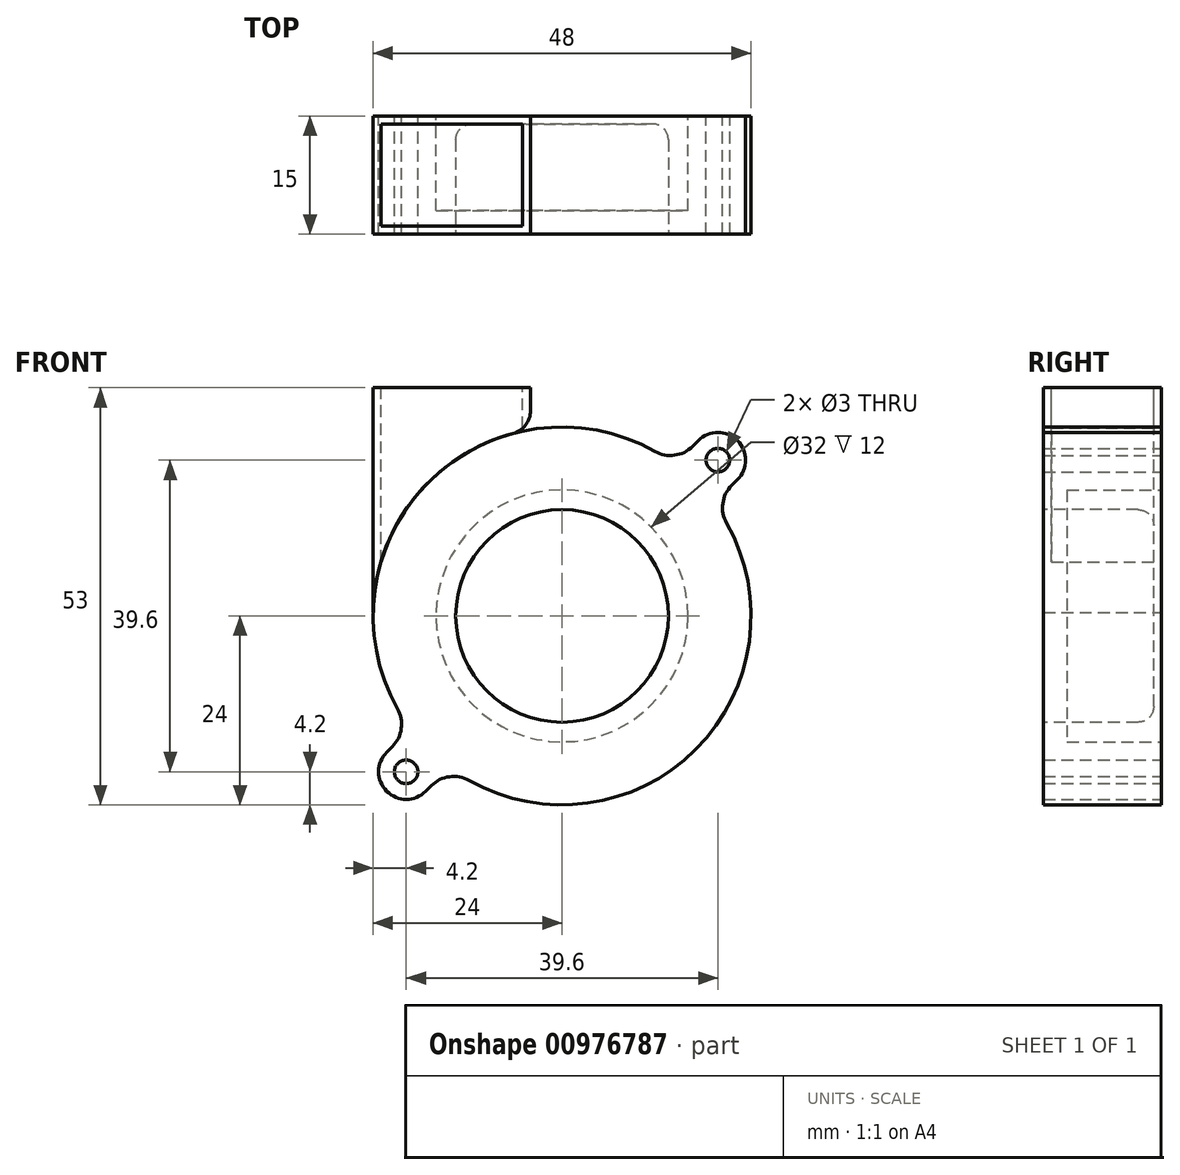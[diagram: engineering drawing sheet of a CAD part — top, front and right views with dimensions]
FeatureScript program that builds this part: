
annotation { "Feature Type Name" : "Feature", "Feature Type Description" : "" }
export const myFeature = defineFeature(function(context is Context, id is Id, definition is map)
    precondition{}
    {
        {
            var Q0;
            Q0=qCreatedBy(makeId("Front.planeOp"),FACE);
            var sketch = newSketch(context, id + "F0", { "sketchPlane" : qUnion([Q0])});
            skArc(sketch, "E0", {"start": v(-11.8, -20.9) * mm, "mid": v(16.97, -16.97) * mm, "end": v(20.9, 11.8) * mm});
            skLineSegment(sketch, "E1", {"start": v(-38.26, -38.26) * mm, "end": v(35.98, 35.98) * mm, "construction": true});
            skCircle(sketch, "E2", {"center": v(-19.8, -19.8) * mm, "radius": 1.5 * mm});
            skCircle(sketch, "E3", {"center": v(19.8, 19.8) * mm, "radius": 1.5 * mm});
            skArc(sketch, "E4", {"start": v(-22.27, -17.32) * mm, "mid": v(-22.27, -22.27) * mm, "end": v(-17.32, -22.27) * mm});
            skArc(sketch, "E5", {"start": v(22.27, 17.32) * mm, "mid": v(22.27, 22.27) * mm, "end": v(17.32, 22.27) * mm});
            skLineSegment(sketch, "E6", {"start": v(-17.32, -22.27) * mm, "end": v(-16.6, -21.55) * mm});
            skLineSegment(sketch, "E7", {"start": v(-22.27, -17.32) * mm, "end": v(-21.55, -16.6) * mm});
            skLineSegment(sketch, "E8.trimOffspring", {"start": v(16.6, 21.55) * mm, "end": v(17.32, 22.27) * mm});
            skLineSegment(sketch, "E9.trimOffspring", {"start": v(21.55, 16.6) * mm, "end": v(22.27, 17.32) * mm});
            skArc(sketch, "E10.trimOffspring", {"start": v(11.8, 20.9) * mm, "mid": v(-16.97, 16.97) * mm, "end": v(-20.9, -11.8) * mm});
            skPoint(sketch, "E11.visualSharp", {"position": v(-14.31, -19.26) * mm});
            skArc(sketch, "E11.filletArc", {"start": v(-11.8, -20.9) * mm, "mid": v(-14.31, -20.42) * mm, "end": v(-16.6, -21.55) * mm});
            skPoint(sketch, "E12.visualSharp", {"position": v(-19.26, -14.31) * mm});
            skArc(sketch, "E12.filletArc", {"start": v(-21.55, -16.6) * mm, "mid": v(-20.42, -14.31) * mm, "end": v(-20.9, -11.8) * mm});
            skPoint(sketch, "E13.visualSharp", {"position": v(19.26, 14.31) * mm});
            skArc(sketch, "E13.filletArc", {"start": v(21.55, 16.6) * mm, "mid": v(20.42, 14.31) * mm, "end": v(20.9, 11.8) * mm});
            skPoint(sketch, "E14.visualSharp", {"position": v(14.31, 19.26) * mm});
            skArc(sketch, "E14.filletArc", {"start": v(11.8, 20.9) * mm, "mid": v(14.31, 20.42) * mm, "end": v(16.6, 21.55) * mm});
            skSolve(sketch);
        }
        {
            var Q0;
            Q0 = qSketchRegion(id + "F0", true);
            extrude(context, id + "F1", {"entities" : qUnion([Q0]), "endBound" : BoundingType.SYMMETRIC, "depth" : 15 * mm, "offsetDistance" : 25 * mm});
        }
        {
            var Q0;
            Q0=qCreatedBy(makeId("Top.planeOp"),FACE);
            cPlane(context, id + "F2", {"entities" : qUnion([Q0]), "cplaneType" : CPlaneType.OFFSET, "offset" : 29 * mm, "width" : 150 * mm, "height" : 150 * mm});
        }
        {
            var Q0;
            Q0=qCreatedBy(id+"F2.planeOp",FACE);
            var sketch = newSketch(context, id + "F3", { "sketchPlane" : qUnion([Q0])});
            skLineSegment(sketch, "E15.bottom", {"start": v(-4, 7.5) * mm, "end": v(-24, 7.5) * mm});
            skLineSegment(sketch, "E15.top", {"start": v(-4, -7.5) * mm, "end": v(-24, -7.5) * mm});
            skLineSegment(sketch, "E15.left", {"start": v(-4, 7.5) * mm, "end": v(-4, -7.5) * mm});
            skLineSegment(sketch, "E15.right", {"start": v(-24, 7.5) * mm, "end": v(-24, -7.5) * mm});
            skPoint(sketch, "E15.middle", {"position": v(-14, 0) * mm});
            skSolve(sketch);
        }
        {
            var Q0;
            Q0 = qSketchRegion(id + "F3", true);
            var Q1;
            Q1=makeQuery(id+"F1.opExtrude","SWEPT_FACE",FACE,{"disambiguationData":[OSD([sQuery(id+"F0.wireOp",EDGE,"E0")])]});
            extrude(context, id + "F4", {"entities" : qUnion([Q0]), "operationType" : NewBodyOperationType.ADD, "endBound" : BoundingType.UP_TO_SURFACE, "oppositeDirection" : true, "depth" : 25 * mm, "endBoundEntityFace" : qUnion([Q1]), "offsetDistance" : 25 * mm});
        }
        {
            var Q0;
            Q0=makeQuery(id+"F1.opExtrude","CAP_FACE",FACE,{"disambiguationData":[OSD([sQuery(id+"F0.wireOp",EDGE,"E0")])],"isStart":true});
            var sketch = newSketch(context, id + "F5", { "sketchPlane" : qUnion([Q0])});
            skCircle(sketch, "E16", {"center": v(0, 0) * mm, "radius": 16 * mm});
            skSolve(sketch);
        }
        {
            var Q0;
            Q0 = qSketchRegion(id + "F5", true);
            extrude(context, id + "F6", {"entities" : qUnion([Q0]), "operationType" : NewBodyOperationType.REMOVE, "oppositeDirection" : true, "depth" : 12 * mm, "offsetDistance" : 25 * mm});
        }
        {
            var Q0;
            Q0=makeQuery(id+"F3.imprint","IMPRINT",FACE,{"disambiguationData":[TD([[makeQuery(id+"F3.imprint","IMPRINT",EDGE,{"derivedFrom":sQuery(id+"F3.wireOp",EDGE,"E15.bottom")}),1.0]])]});
            var sketch = newSketch(context, id + "F7", { "sketchPlane" : qUnion([Q0])});
            skLineSegment(sketch, "E17.0", {"start": v(-23, -6.5) * mm, "end": v(-5, -6.5) * mm});
            skLineSegment(sketch, "E17.1", {"start": v(-23, 6.5) * mm, "end": v(-23, -6.5) * mm});
            skLineSegment(sketch, "E17.2", {"start": v(-5, 6.5) * mm, "end": v(-23, 6.5) * mm});
            skLineSegment(sketch, "E17.3", {"start": v(-5, -6.5) * mm, "end": v(-5, 6.5) * mm});
            skSolve(sketch);
        }
        {
            var Q0;
            Q0=makeQuery(id+"F7.imprint","IMPRINT",FACE,{"disambiguationData":[TD([[makeQuery(id+"F7.imprint","IMPRINT",EDGE,{"derivedFrom":sQuery(id+"F7.wireOp",EDGE,"E17.0")}),1.0]])]});
            var Q1;
            Q1=makeQuery(id+"F1.opExtrude","SWEPT_FACE",FACE,{"disambiguationData":[OSD([sQuery(id+"F0.wireOp",EDGE,"E0")])]});
            extrude(context, id + "F8", {"entities" : qUnion([Q0]), "operationType" : NewBodyOperationType.REMOVE, "endBound" : BoundingType.UP_TO_SURFACE, "oppositeDirection" : true, "depth" : 25 * mm, "endBoundEntityFace" : qUnion([Q1]), "offsetDistance" : 25 * mm});
        }
        {
            var Q0;
            Q0=makeQuery(id+"F4.opExtrude","CAP_EDGE",EDGE,{"disambiguationData":[OSD([sQuery(id+"F3.wireOp",EDGE,"E15.left")])],"isStart":false});
            fillet(context, id + "F9", {"entities" : qUnion([Q0]), "radius" : 3 * mm, "tangentPropagation" : true, "allowEdgeOverflow" : false});
        }
        {
            var Q0;
            Q0=makeQuery(id+"F4.boolean.opBoolean","MERGE",FACE,{"derivedFrom":[makeQuery(id+"F1.opExtrude","CAP_FACE",FACE,{"disambiguationData":[OSD([sQuery(id+"F0.wireOp",EDGE,"E0"),sQuery(id+"F0.wireOp",EDGE,"E2"),sQuery(id+"F0.wireOp",EDGE,"E3"),sQuery(id+"F0.wireOp",EDGE,"E4"),sQuery(id+"F0.wireOp",EDGE,"E5"),sQuery(id+"F0.wireOp",EDGE,"E6"),sQuery(id+"F0.wireOp",EDGE,"E7"),sQuery(id+"F0.wireOp",EDGE,"E8.trimOffspring"),sQuery(id+"F0.wireOp",EDGE,"E9.trimOffspring"),sQuery(id+"F0.wireOp",EDGE,"E10.trimOffspring"),sQuery(id+"F0.wireOp",EDGE,"E11.filletArc"),sQuery(id+"F0.wireOp",EDGE,"E12.filletArc"),sQuery(id+"F0.wireOp",EDGE,"E13.filletArc"),sQuery(id+"F0.wireOp",EDGE,"E14.filletArc")])],"isStart":false}),makeQuery(id+"F4.opExtrude","SWEPT_FACE",FACE,{"disambiguationData":[OSD([sQuery(id+"F3.wireOp",EDGE,"E15.top")])]})]});
            var sketch = newSketch(context, id + "F10", { "sketchPlane" : qUnion([Q0])});
            skCircle(sketch, "E18", {"center": v(0, 0) * mm, "radius": 13.5 * mm});
            skSolve(sketch);
        }
        {
            var Q0;
            Q0 = qSketchRegion(id + "F10", true);
            var Q1;
            Q1 = qConstructionFilter(qBodyType(qCreatedBy(id + "F10" ,EDGE), BodyType.WIRE), ConstructionObject.NO);
            extrude(context, id + "F11", {"entities" : qUnion([Q0]), "surfaceEntities" : qUnion([Q1]), "oppositeDirection" : true, "depth" : 14 * mm, "offsetDistance" : 25 * mm});
        }
        {
            var Q0;
            Q0=makeQuery(id+"F11.opExtrude","CAP_EDGE",EDGE,{"disambiguationData":[OSD([sQuery(id+"F10.wireOp",EDGE,"E18")])],"isStart":false});
            fillet(context, id + "F12", {"entities" : qUnion([Q0]), "radius" : 2 * mm, "tangentPropagation" : true, "allowEdgeOverflow" : false});
        }
    });
